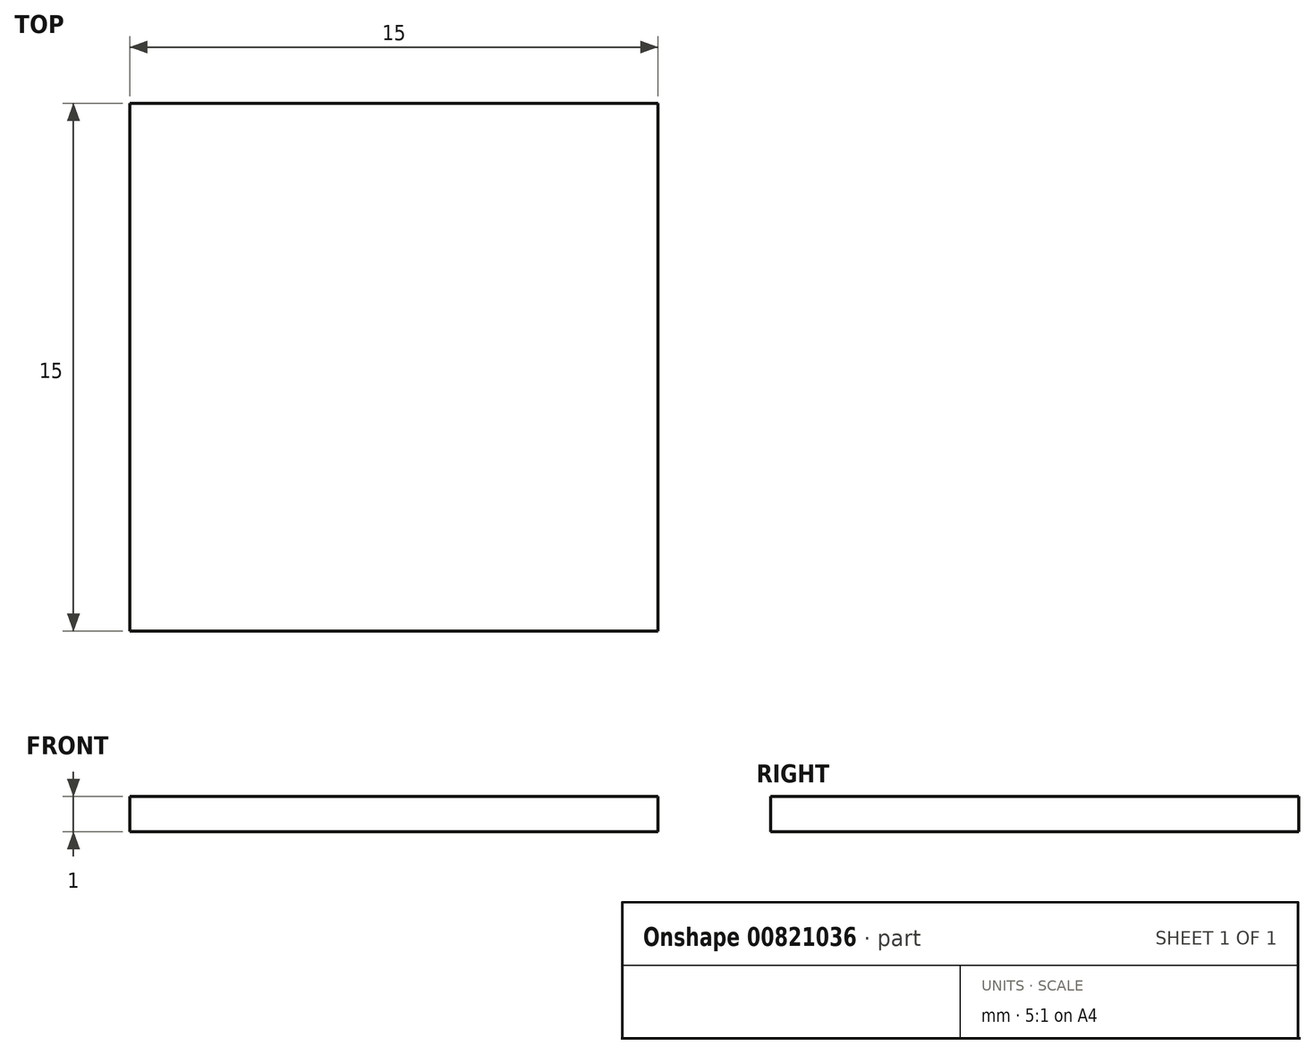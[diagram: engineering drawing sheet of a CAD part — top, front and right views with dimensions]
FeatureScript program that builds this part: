
annotation { "Feature Type Name" : "Feature", "Feature Type Description" : "" }
export const myFeature = defineFeature(function(context is Context, id is Id, definition is map)
    precondition{}
    {
        {
            var Q0;
            Q0=qCreatedBy(makeId("Top.planeOp"),FACE);
            var sketch = newSketch(context, id + "F0", { "sketchPlane" : qUnion([Q0])});
            skLineSegment(sketch, "E0.bottom", {"start": v(7.5, 7.5) * mm, "end": v(-7.5, 7.5) * mm});
            skLineSegment(sketch, "E0.top", {"start": v(7.5, -7.5) * mm, "end": v(-7.5, -7.5) * mm});
            skLineSegment(sketch, "E0.left", {"start": v(7.5, 7.5) * mm, "end": v(7.5, -7.5) * mm});
            skLineSegment(sketch, "E0.right", {"start": v(-7.5, 7.5) * mm, "end": v(-7.5, -7.5) * mm});
            skPoint(sketch, "E0.middle", {"position": v(0, 0) * mm});
            skSolve(sketch);
        }
        {
            var Q0;
            Q0=makeQuery(id+"F0.imprint","IMPRINT",FACE,{"disambiguationData":[TD([[makeQuery(id+"F0.imprint","IMPRINT",EDGE,{"derivedFrom":sQuery(id+"F0.wireOp",EDGE,"E0.bottom")}),1.0]])]});
            extrude(context, id + "F1", {"entities" : qUnion([Q0]), "depth" : 1 * mm, "offsetDistance" : 25 * mm});
        }
    });
